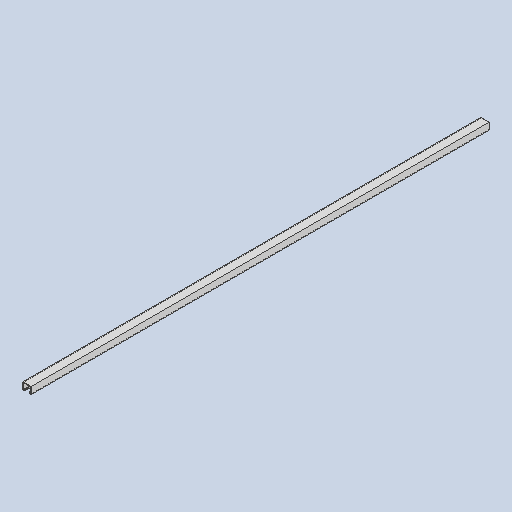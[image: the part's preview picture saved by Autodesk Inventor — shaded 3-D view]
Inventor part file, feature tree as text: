
AUTODESK INVENTOR PART (.ipt)
format: ipt  version: 2023 (Build 270158030, 158C)  size: 101,888 bytes
history: native  units: in
note: dims shown in document units (in); Inventor stores cm internally (conversion verified against a paired STEP export)
features: extrude x1, sketch x1
ambient origin geometry x8: Origin, YZ Plane, XZ Plane, XY Plane, X Axis, Y Axis, Z Axis, Center Point
bodies: Solid1 (feature_tree)
feature tree (2):
  extrude  "Extrusion1"  Depth=1.375in
  sketch  "Sketch1"  dims[d0=1.625in d1=1.375in d4=0.375in d5=0.2812in d6=0.1024in d7=0.1024in d8=0.1024in d9=0.1024in d11=0.1024in d12=0.1024in d13=0.2812in d14=0.1024in d15=90.0in d16=0.0in]
